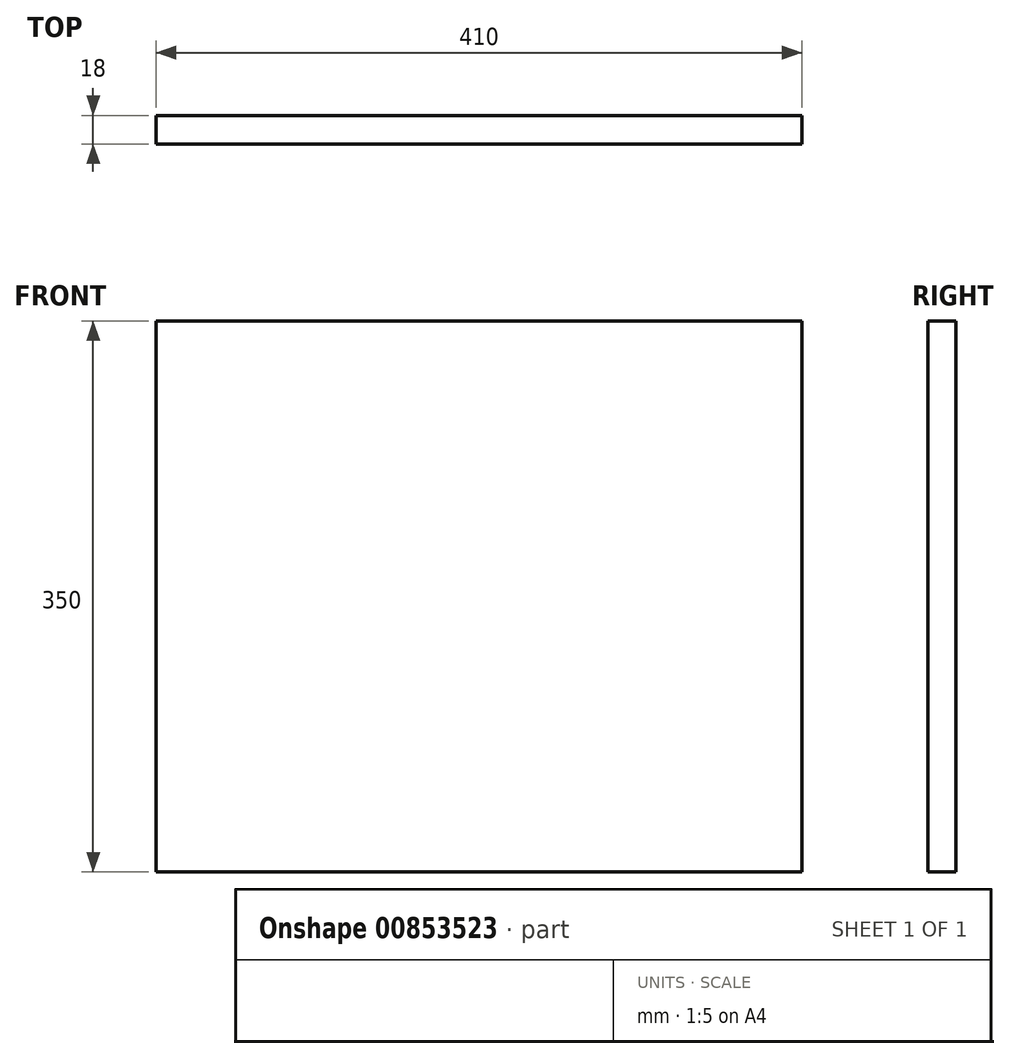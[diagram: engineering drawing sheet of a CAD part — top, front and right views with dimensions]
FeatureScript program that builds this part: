
annotation { "Feature Type Name" : "Feature", "Feature Type Description" : "" }
export const myFeature = defineFeature(function(context is Context, id is Id, definition is map)
    precondition{}
    {
        {
            var Q0;
            Q0=qCreatedBy(makeId("Front.planeOp"),FACE);
            var sketch = newSketch(context, id + "F0", { "sketchPlane" : qUnion([Q0])});
            skLineSegment(sketch, "E0.bottom", {"start": v(211.58, 175) * mm, "end": v(-198.42, 175) * mm});
            skLineSegment(sketch, "E0.top", {"start": v(211.58, -175) * mm, "end": v(-198.42, -175) * mm});
            skLineSegment(sketch, "E0.left", {"start": v(211.58, 175) * mm, "end": v(211.58, -175) * mm});
            skLineSegment(sketch, "E0.right", {"start": v(-198.42, 175) * mm, "end": v(-198.42, -175) * mm});
            skPoint(sketch, "E0.middle", {"position": v(6.58, 0) * mm});
            skSolve(sketch);
        }
        {
            var Q0;
            Q0 = qSketchRegion(id + "F0", true);
            extrude(context, id + "F1", {"entities" : qUnion([Q0]), "depth" : 18 * mm, "offsetDistance" : 25 * mm});
        }
    });
